# Revit family: Grohe_ShowerHead_SmartActive310_22123KF0
name_source: partatom
category: Plumbing Fixtures
units: mm (PartAtom-declared; Revit-internal decimal feet)

## family parameters
Cut with Voids When Loaded = No
Host = Face
OmniClass Number = 23.45.05.00
OmniClass Title = Sanitary Equipment
Part Type = Normal
Room Calculation Point = No
Round Connector Dimension = Use Diameter
Shared = No

## types (1)
- RAINSHOWER SMARTACTIVE 310 Head Shower Set (22123KF0)
    Assembly Code = D2010
    AssetType = Fixed
    BIMObjectName = Grohe_ShowerHead_SmartActive310_22123KF0
    CO2NeutralProduction = GROHE is one of the first leading manufacturer within the sanitary industry having a CO2-neutral production.
    CW Connection = Yes
    ClassificationName = Uniclass2015
    ClassificationValue = Pr_40_20_87_76
    Color = Matt Black
    Cost = 0 $
    Default Elevation = 0 mm  [stored 0 ft]
    Description = RAINSHOWER SMARTACTIVE 310 Head Shower Set
    DimensionsDocumentLink = https://cdn.cloud.grohe.com
    DocumentationCertificates = https://www.bimstore.co
    DocumentationInstallationGuide = https://www.bimstore.co
    DocumentationLiterature = https://www.bimstore.co
    DocumentationMaintenance = https://www.bimstore.co
    DocumentationTechnical = https://www.bimstore.co
    DurationUnit = Years
    EF000008 = 310 mm  [stored 1.01706 ft]
    EF000040 = 64 mm  [stored 0.209974 ft]
    EF000049 = 585 mm  [stored 1.91929 ft]
    EF000051 = Cascade spout
    EF000303 = 430 mm
    EF000443 = Other
    EF000551 = 310 mm  [stored 1.01706 ft]
    EF000653 = TRUE
    EF001707 = 70 °C
    EF002671 = Other
    EF006114 = FALSE
    EF012753 = 44.0
    EF015301 = TRUE
    EF015309 = 400 mm  [stored 1.31234 ft]
    EF021040 = 2
    EF021480 = TRUE
    EF022042 = None
    EF022221 = FALSE
    EF022222 = FALSE
    EF022223 = FALSE
    EF022224 = TRUE
    EF022726 = Internal thread
    EF023452 = Other
    EF023686 = not applicable
    Ecojoy = No
    ExpectedLife = 0
    FullRecyclabilityOfPlastic = All plastic components are fully recyclable
    GROHESocialCommittment = green.grohe.com/social_engagement
    GROHESustainability = green.grohe.com
    HW Connection = Yes
    IfcExportAs = IfcPipeFitting
    IfcExportType = IfcPipeFittingType
    Keynote = N13
    Manufacturer = Grohe
    ManufacturerName = Grohe
    Model = RAINSHOWER SMARTACTIVE 310 Head Shower Set
    ModelNumber = 22123KF0
    ModelReference = RAINSHOWER SMARTACTIVE 310 Head Shower Set
    NBSDescription = Shower heads
    NBSObjectName = Grohe - Shower heads
    NBSReference = 45-35-70/333
    NominalDepth = 0 mm  [stored 0 ft]
    NominalHeight = 0 mm  [stored 0 ft]
    NominalLength = 0 mm  [stored 0 ft]
    PQDiagramLink = https://cdn.cloud.grohe.com
    PrimaryMaterial = Grohe_MattBlack
    ProductDescription = consisting of:

head shower Rainshower SmartActive 310

2 spray patterns:

GROHE PureRain, ActiveRain

horizontal 430 mm shower arm

GROHE DreamSpray perfect spray pattern

GROHE Long-Life Shine finish

SpeedClean anti-limescale system

Inner WaterGuide for a longer life

requires rough-in set 26 483 000 or 26 484 000 - to be ordered separately
    ProductNumber = 22123KF0
    ProductPageURL = https://www.grohe.co.uk
    ProductShortText = Head shower set 430 mm, 2 sprays
    ProductType = Shower Set
    ProductionYear = 2023
    SustainabilityAward = green.grohe.com/awards
    SustainabilityReport = green.grohe.com/reporting
    TPIDocumentLink = https://cdn.cloud.grohe.com
    Type Comments = RAINSHOWER SMARTACTIVE 310 Head Shower Set
    TypeName = RAINSHOWER SMARTACTIVE 310 Head Shower Set
    URL = https://www.grohe.co.uk
    Vent Connection = No
    WarrantyDurationLabor = 0
    WarrantyDurationParts = 0
    WarrantyDurationUnit = Years
    Waste Connection = No
    _BSBibleVersion = 17
    _BimSpecGuid = 0
    _CurrentRevision = 1
    _DistributedBy = https://www.bimstore.co
    _ObjectUserGuide = https://www.bimstore.co

note: [stored X ft] marks values corroborated as IEEE doubles in the binary element streams (Revit-internal decimal feet)

## geometry (parser evidence)
native form markers: Sweep x1
no freeform markers — native parametric forms only
